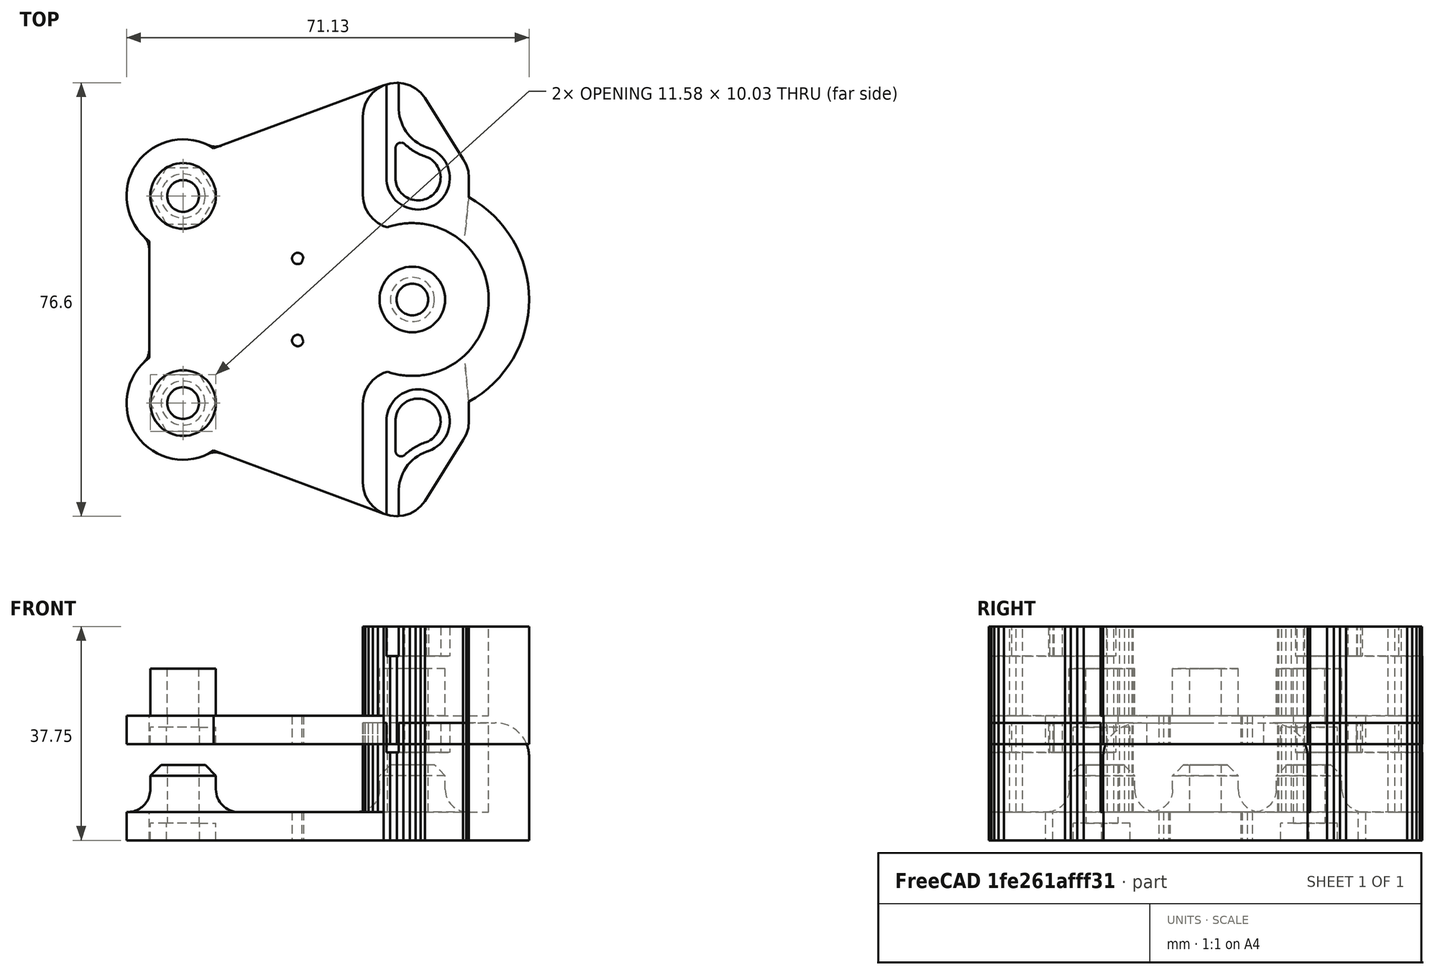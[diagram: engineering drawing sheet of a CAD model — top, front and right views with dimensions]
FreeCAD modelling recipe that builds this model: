
FCSTD DOCUMENT  (FreeCAD 0.19R24267 +99 (Git))
Label: carroX
License: All rights reserved
LicenseURL: http://en.wikipedia.org/wiki/All_rights_reserved
objects: Part::Feature×137, Part::Part2DObjectPython×10, Part::Cylinder×10, Part::FeaturePython×8, Part::Fillet×8, Part::Cut×7, Part::MultiFuse×6, Part::Extrusion×5, Part::Fuse×3, Part::Prism×3, Part::Box×1, App::DocumentObjectGroupPython×1, Part::Mirroring×1, Part::Refine×1, Part::Chamfer×1
note: 201 computed .brp shape members not serialized (recipe doc carries the construction recipe); baked Part::Feature solids carry a one-line shape summary decoded from their .brp

FEATURE [Part::Feature] polygon
  shape: bbox 44.5 x 64.6 x 2e-07 mm, 1 faces, 0 solids (baked)
FEATURE [Part::Part2DObjectPython] circle  # Draft 2D object (typed FeaturePython)
  Area = 113.097
  FirstAngle = 0
  LastAngle = 0
  MakeFace = true
  Radius = 6
FEATURE [Part::FeaturePython] minkowski  # WARN: FeaturePython — macro-defined, semantics opaque (R4)
  Arguments = {'convexity': '0'}
  Children = -> [polygon,circle]
  Operation = minkowski
FEATURE [Part::Part2DObjectPython] circle001  # Draft 2D object (typed FeaturePython)
  Area = 314.159
  FirstAngle = 0
  LastAngle = 0
  MakeFace = true
  Placement = pos=(-20.25,-18.3,0) rot=(0,0,1;0rad)
  Radius = 10
FEATURE [Part::Part2DObjectPython] circle002  # Draft 2D object (typed FeaturePython)
  Area = 314.159
  FirstAngle = 0
  LastAngle = 0
  MakeFace = true
  Placement = pos=(-20.25,18.3,0) rot=(0,0,1;0rad)
  Radius = 10
FEATURE [Part::MultiFuse] union
  Shapes = -> [minkowski,circle001,circle002]
FEATURE [Part::Part2DObjectPython] circle003  # Draft 2D object (typed FeaturePython)
  Area = 24.6301
  FirstAngle = 0
  LastAngle = 0
  MakeFace = true
  Placement = pos=(-20.25,-18.3,0) rot=(0,0,1;0rad)
  Radius = 2.8
FEATURE [Part::Part2DObjectPython] circle004  # Draft 2D object (typed FeaturePython)
  Area = 24.6301
  FirstAngle = 0
  LastAngle = 0
  MakeFace = true
  Placement = pos=(20.25,0,0) rot=(0,0,1;0rad)
  Radius = 2.8
FEATURE [Part::Part2DObjectPython] circle005  # Draft 2D object (typed FeaturePython)
  Area = 24.6301
  FirstAngle = 0
  LastAngle = 0
  MakeFace = true
  Placement = pos=(-20.25,18.3,0) rot=(0,0,1;0rad)
  Radius = 2.8
FEATURE [Part::Part2DObjectPython] circle006  # Draft 2D object (typed FeaturePython)
  Area = 3.14159
  FirstAngle = 0
  LastAngle = 0
  MakeFace = true
  Placement = pos=(0,7.25,0) rot=(0,0,1;0rad)
  Radius = 1
FEATURE [Part::Part2DObjectPython] circle007  # Draft 2D object (typed FeaturePython)
  Area = 3.14159
  FirstAngle = 0
  LastAngle = 0
  MakeFace = true
  Placement = pos=(0,-7.25,0) rot=(0,0,1;0rad)
  Radius = 1
FEATURE [Part::MultiFuse] union001
  Shapes = -> [circle003,circle004,circle005,circle006,circle007]
FEATURE [Part::Cut] difference
  Base = -> union
  Tool = -> union001
FEATURE [Part::FeaturePython] RefineLinearExtrude  # WARN: FeaturePython — macro-defined, semantics opaque (R4)
  Base = -> difference
FEATURE [Part::Extrusion] LinearExtrude
  Base = -> RefineLinearExtrude
  Dir = (0,0,5)
  DirMode = 0
  FaceMakerClass = Part::FaceMakerBullseye
  LengthFwd = 0
  LengthRev = 0
  Solid = false
  Symmetric = false
FEATURE [Part::Feature] polygon001
  shape: bbox 6.75 x 13.8 x 2e-07 mm, 1 faces, 0 solids (baked)
FEATURE [Part::Part2DObjectPython] circle008  # Draft 2D object (typed FeaturePython)
  Area = 113.097
  FirstAngle = 0
  LastAngle = 0
  MakeFace = true
  Radius = 6
FEATURE [Part::FeaturePython] minkowski001  # WARN: FeaturePython — macro-defined, semantics opaque (R4)
  Arguments = {'convexity': '0'}
  Children = -> [polygon001,circle008]
  Operation = minkowski
FEATURE [Part::FeaturePython] RefineLinearExtrude001  # WARN: FeaturePython — macro-defined, semantics opaque (R4)
  Base = -> minkowski001
FEATURE [Part::Extrusion] LinearExtrude001
  Base = -> RefineLinearExtrude001
  Dir = (0,0,20.75)
  DirMode = 0
  FaceMakerClass = Part::FaceMakerBullseye
  LengthFwd = 0
  LengthRev = 0
  Solid = false
  Symmetric = false
FEATURE [Part::Feature] polygon002
  shape: bbox 6.75 x 13.8 x 2e-07 mm, 1 faces, 0 solids (baked)
FEATURE [Part::Part2DObjectPython] circle009  # Draft 2D object (typed FeaturePython)
  Area = 113.097
  FirstAngle = 0
  LastAngle = 0
  MakeFace = true
  Radius = 6
FEATURE [Part::FeaturePython] minkowski002  # WARN: FeaturePython — macro-defined, semantics opaque (R4)
  Arguments = {'convexity': '0'}
  Children = -> [polygon002,circle009]
  Operation = minkowski
FEATURE [Part::FeaturePython] RefineLinearExtrude002  # WARN: FeaturePython — macro-defined, semantics opaque (R4)
  Base = -> minkowski002
FEATURE [Part::Extrusion] LinearExtrude002
  Base = -> RefineLinearExtrude002
  Dir = (0,0,20.75)
  DirMode = 0
  FaceMakerClass = Part::FaceMakerBullseye
  LengthFwd = 0
  LengthRev = 0
  Solid = false
  Symmetric = false
FEATURE [Part::Fuse] union002
  Base = -> LinearExtrude001
  Tool = -> LinearExtrude002
FEATURE [Part::Cylinder] cylinder
  Angle = 360
  AttacherType = Attacher::AttachEngine3D
  Height = 60
  Placement = pos=(20.25,0,0) rot=(0,0,1;0rad)
  Radius = 13.5
FEATURE [Part::Cut] difference001
  Base = -> union002
  Tool = -> cylinder
FEATURE [Part::Cylinder] cylinder001
  Angle = 360
  AttacherType = Attacher::AttachEngine3D
  Height = 13.3
  Radius = 5.8
FEATURE [Part::Cylinder] cylinder002
  Angle = 360
  AttacherType = Attacher::AttachEngine3D
  Height = 53.2
  Placement = pos=(0,0,-26.6) rot=(0,0,1;0rad)
  Radius = 2.8
FEATURE [Part::Cut] difference002
  Base = -> cylinder001
  Placement = pos=(-20.25,-18.3,0) rot=(0,0,1;0rad)
  Tool = -> cylinder002
FEATURE [Part::Cylinder] cylinder003
  Angle = 360
  AttacherType = Attacher::AttachEngine3D
  Height = 13.3
  Radius = 5.8
FEATURE [Part::Cylinder] cylinder004
  Angle = 360
  AttacherType = Attacher::AttachEngine3D
  Height = 53.2
  Placement = pos=(0,0,-26.6) rot=(0,0,1;0rad)
  Radius = 2.8
FEATURE [Part::Cut] difference003
  Base = -> cylinder003
  Placement = pos=(-20.25,18.3,0) rot=(0,0,1;0rad)
  Tool = -> cylinder004
FEATURE [Part::Cylinder] cylinder005
  Angle = 360
  AttacherType = Attacher::AttachEngine3D
  Height = 13.3
  Radius = 5.8
FEATURE [Part::Cylinder] cylinder006
  Angle = 360
  AttacherType = Attacher::AttachEngine3D
  Height = 53.2
  Placement = pos=(0,0,-26.6) rot=(0,0,1;0rad)
  Radius = 2.8
FEATURE [Part::Cut] difference004
  Base = -> cylinder005
  Placement = pos=(20.25,0,0) rot=(0,0,1;0rad)
  Tool = -> cylinder006
FEATURE [Part::Cylinder] cylinder007
  Angle = 360
  AttacherType = Attacher::AttachEngine3D
  Height = 20.75
  Radius = 20.625
FEATURE [Part::Cylinder] cylinder008
  Angle = 360
  AttacherType = Attacher::AttachEngine3D
  Height = 1000
  Placement = pos=(0,0,4.99) rot=(0,0,1;0rad)
  Radius = 13.5
FEATURE [Part::Box] cube
  AttacherType = Attacher::AttachEngine3D
  Height = 1000
  Length = 1000
  Placement = pos=(-1000,-500,0) rot=(0,0,1;0rad)
  Width = 1000
FEATURE [Part::Fuse] union003
  Base = -> cylinder008
  Tool = -> cube
FEATURE [Part::Cut] difference005
  Base = -> cylinder007
  Placement = pos=(20.25,0,0) rot=(0,0,1;0rad)
  Tool = -> union003
FEATURE [Part::MultiFuse] union004
  Shapes = -> [LinearExtrude,difference001,difference002,difference003,difference004,difference005]
FEATURE [Part::Prism] prism
  AttacherType = Attacher::AttachEngine3D
  Circumradius = 5.79
  FirstAngle = 0
  Height = 6
  Placement = pos=(-20.25,-18.3,-3) rot=(0,0,1;0rad)
  Polygon = 6
  SecondAngle = 0
FEATURE [Part::Prism] prism001
  AttacherType = Attacher::AttachEngine3D
  Circumradius = 5.79
  FirstAngle = 0
  Height = 6
  Placement = pos=(-20.25,18.3,-3) rot=(0,0,1;0rad)
  Polygon = 6
  SecondAngle = 0
FEATURE [Part::Prism] prism002
  AttacherType = Attacher::AttachEngine3D
  Circumradius = 5.79
  FirstAngle = 0
  Height = 6
  Placement = pos=(20.25,0,-3) rot=(0,0,1;0rad)
  Polygon = 6
  SecondAngle = 0
FEATURE [Part::MultiFuse] Group
  Shapes = -> [prism,prism001,prism002]
FEATURE [App::DocumentObjectGroupPython] LayerContainer  label="Capas"  # scripted group (container) (typed FeaturePython)
FEATURE [Part::Feature] Line
  shape: bbox 25.93 x 2e-07 x 2e-07 mm, 0 faces, 0 solids (baked)
FEATURE [Part::Feature] Line001
  shape: bbox 5.23 x 0.01028 x 2e-07 mm, 0 faces, 0 solids (baked)
FEATURE [Part::Feature] Line002
  shape: bbox 13.12 x 2e-07 x 2e-07 mm, 0 faces, 0 solids (baked)
FEATURE [Part::Feature] Line003
  shape: bbox 46.78 x 2e-07 x 2e-07 mm, 0 faces, 0 solids (baked)
FEATURE [Part::Feature] Line004
  shape: bbox 46.66 x 2e-07 x 2e-07 mm, 0 faces, 0 solids (baked)
FEATURE [Part::Feature] Line005
  shape: bbox 2e-07 x 2.2 x 2e-07 mm, 0 faces, 0 solids (baked)
FEATURE [Part::Feature] Arc
  shape: bbox 7.844 x 7.989 x 2e-07 mm, 0 faces, 0 solids (baked)
FEATURE [Part::Feature] Arc001
  shape: bbox 0.9979 x 1.743 x 2e-07 mm, 0 faces, 0 solids (baked)
FEATURE [Part::Feature] Arc002
  shape: bbox 10.99 x 11.2 x 2e-07 mm, 0 faces, 0 solids (baked)
FEATURE [Part::Feature] Arc003
  shape: bbox 2.238 x 3.76 x 2e-07 mm, 0 faces, 0 solids (baked)
FEATURE [Part::Feature] Arc004
  shape: bbox 7.439 x 5.334 x 2e-07 mm, 0 faces, 0 solids (baked)
FEATURE [Part::Feature] dxf_ToyRepCart_all
  Placement = pos=(0,0,0) rot=(0,0,1;1.5708rad)
  shape: bbox 11.2 x 78.19 x 2e-07 mm, 1 faces, 0 solids (baked)
FEATURE [Part::FeaturePython] RefineLinearExtrude003  # WARN: FeaturePython — macro-defined, semantics opaque (R4)
  Base = -> dxf_ToyRepCart_all
FEATURE [Part::Extrusion] LinearExtrude003
  Base = -> RefineLinearExtrude003
  Dir = (0,0,100)
  DirMode = 0
  FaceMakerClass = Part::FaceMakerBullseye
  LengthFwd = 0
  LengthRev = 0
  Placement = pos=(21.25,-21.5,15.55) rot=(0,0,1;0rad)
  Solid = false
  Symmetric = false
FEATURE [Part::Feature] Line006
  shape: bbox 25.93 x 2e-07 x 2e-07 mm, 0 faces, 0 solids (baked)
FEATURE [Part::Feature] Line007
  shape: bbox 5.23 x 0.01028 x 2e-07 mm, 0 faces, 0 solids (baked)
FEATURE [Part::Feature] Line008
  shape: bbox 13.12 x 2e-07 x 2e-07 mm, 0 faces, 0 solids (baked)
FEATURE [Part::Feature] Line009
  shape: bbox 46.78 x 2e-07 x 2e-07 mm, 0 faces, 0 solids (baked)
FEATURE [Part::Feature] Line010
  shape: bbox 46.66 x 2e-07 x 2e-07 mm, 0 faces, 0 solids (baked)
FEATURE [Part::Feature] Line011
  shape: bbox 2e-07 x 2.2 x 2e-07 mm, 0 faces, 0 solids (baked)
FEATURE [Part::Feature] Arc005
  shape: bbox 7.844 x 7.989 x 2e-07 mm, 0 faces, 0 solids (baked)
FEATURE [Part::Feature] Arc006
  shape: bbox 0.9979 x 1.743 x 2e-07 mm, 0 faces, 0 solids (baked)
FEATURE [Part::Feature] Arc007
  shape: bbox 10.99 x 11.2 x 2e-07 mm, 0 faces, 0 solids (baked)
FEATURE [Part::Feature] Arc008
  shape: bbox 2.238 x 3.76 x 2e-07 mm, 0 faces, 0 solids (baked)
FEATURE [Part::Feature] Arc009
  shape: bbox 7.439 x 5.334 x 2e-07 mm, 0 faces, 0 solids (baked)
FEATURE [Part::Feature] dxf_ToyRepCart_all001
  Placement = pos=(0,0,0) rot=(0,0,1;1.5708rad)
  shape: bbox 11.2 x 78.19 x 2e-07 mm, 1 faces, 0 solids (baked)
FEATURE [Part::FeaturePython] RefineLinearExtrude004  # WARN: FeaturePython — macro-defined, semantics opaque (R4)
  Base = -> dxf_ToyRepCart_all001
FEATURE [Part::Extrusion] LinearExtrude004
  Base = -> RefineLinearExtrude004
  Dir = (0,0,100)
  DirMode = 0
  FaceMakerClass = Part::FaceMakerBullseye
  LengthFwd = 0
  LengthRev = 0
  Placement = pos=(21.25,-21.5,15.55) rot=(0,0,1;0rad)
  Solid = false
  Symmetric = false
FEATURE [Part::Mirroring] mirr_LinearExtrude004  label="mirrored LinearExtrude004"
  Base = (0,0,0)
  Normal = (0,1,0)
  Source = -> LinearExtrude004
FEATURE [Part::MultiFuse] union005
  Shapes = -> [Group,LinearExtrude003,mirr_LinearExtrude004]
FEATURE [Part::Cut] difference006
  Base = -> union004
  Tool = -> union005
FEATURE [Part::Cylinder] cylinder009
  Angle = 360
  AttacherType = Attacher::AttachEngine3D
  Height = 5
  Placement = pos=(20.25,0,0) rot=(0,0,1;0rad)
  Radius = 20.625
FEATURE [Part::Fuse] Group001
  Base = -> difference006
  Tool = -> cylinder009
FEATURE [Part::Feature] Line012
  shape: bbox 1.171 x 0.1152 x 2e-07 mm, 0 faces, 0 solids (baked)
FEATURE [Part::Feature] Line013
  shape: bbox 1.171 x 0.1152 x 2e-07 mm, 0 faces, 0 solids (baked)
FEATURE [Part::Feature] Line014
  shape: bbox 1.125 x 0.3418 x 2e-07 mm, 0 faces, 0 solids (baked)
FEATURE [Part::Feature] Line015
  shape: bbox 37.75 x 14 x 2e-07 mm, 0 faces, 0 solids (baked)
FEATURE [Part::Feature] Line016
  shape: bbox 1.037 x 0.5537 x 2e-07 mm, 0 faces, 0 solids (baked)
FEATURE [Part::Feature] Line017
  shape: bbox 0.9092 x 0.7471 x 2e-07 mm, 0 faces, 0 solids (baked)
FEATURE [Part::Feature] Line018
  shape: bbox 0.7471 x 0.9092 x 2e-07 mm, 0 faces, 0 solids (baked)
FEATURE [Part::Feature] Line019
  shape: bbox 0.5537 x 1.037 x 2e-07 mm, 0 faces, 0 solids (baked)
FEATURE [Part::Feature] Line020
  shape: bbox 0.3418 x 1.125 x 2e-07 mm, 0 faces, 0 solids (baked)
FEATURE [Part::Feature] Line021
  shape: bbox 0.1152 x 1.171 x 2e-07 mm, 0 faces, 0 solids (baked)
FEATURE [Part::Feature] Line022
  shape: bbox 2e-07 x 36.6 x 2e-07 mm, 0 faces, 0 solids (baked)
FEATURE [Part::Feature] Line023
  shape: bbox 0.1152 x 1.171 x 2e-07 mm, 0 faces, 0 solids (baked)
FEATURE [Part::Feature] Line024
  shape: bbox 0.3418 x 1.125 x 2e-07 mm, 0 faces, 0 solids (baked)
FEATURE [Part::Feature] Line025
  shape: bbox 0.5537 x 1.037 x 2e-07 mm, 0 faces, 0 solids (baked)
FEATURE [Part::Feature] Line026
  shape: bbox 0.7471 x 0.9092 x 2e-07 mm, 0 faces, 0 solids (baked)
FEATURE [Part::Feature] Line027
  shape: bbox 0.9092 x 0.7471 x 2e-07 mm, 0 faces, 0 solids (baked)
FEATURE [Part::Feature] Line028
  shape: bbox 1.037 x 0.5537 x 2e-07 mm, 0 faces, 0 solids (baked)
FEATURE [Part::Feature] Line029
  shape: bbox 37.75 x 14 x 2e-07 mm, 0 faces, 0 solids (baked)
FEATURE [Part::Feature] Line030
  shape: bbox 1.125 x 0.3418 x 2e-07 mm, 0 faces, 0 solids (baked)
FEATURE [Part::Feature] Line031
  shape: bbox 1.171 x 0.1152 x 2e-07 mm, 0 faces, 0 solids (baked)
FEATURE [Part::Feature] Line032
  shape: bbox 1.171 x 0.1152 x 2e-07 mm, 0 faces, 0 solids (baked)
FEATURE [Part::Feature] Line033
  shape: bbox 1.125 x 0.3418 x 2e-07 mm, 0 faces, 0 solids (baked)
FEATURE [Part::Feature] Line034
  shape: bbox 1.037 x 0.5537 x 2e-07 mm, 0 faces, 0 solids (baked)
FEATURE [Part::Feature] Line035
  shape: bbox 0.9092 x 0.7471 x 2e-07 mm, 0 faces, 0 solids (baked)
FEATURE [Part::Feature] Line036
  shape: bbox 0.7471 x 0.9092 x 2e-07 mm, 0 faces, 0 solids (baked)
FEATURE [Part::Feature] Line037
  shape: bbox 6.75 x 10.8 x 2e-07 mm, 0 faces, 0 solids (baked)
FEATURE [Part::Feature] Line038
  shape: bbox 0.5537 x 1.037 x 2e-07 mm, 0 faces, 0 solids (baked)
FEATURE [Part::Feature] Line039
  shape: bbox 0.3418 x 1.125 x 2e-07 mm, 0 faces, 0 solids (baked)
FEATURE [Part::Feature] Line040
  shape: bbox 0.1152 x 1.171 x 2e-07 mm, 0 faces, 0 solids (baked)
FEATURE [Part::Feature] Line041
  shape: bbox 2e-07 x 43 x 2e-07 mm, 0 faces, 0 solids (baked)
FEATURE [Part::Feature] Line042
  shape: bbox 0.1152 x 1.171 x 2e-07 mm, 0 faces, 0 solids (baked)
FEATURE [Part::Feature] Line043
  shape: bbox 0.3418 x 1.125 x 2e-07 mm, 0 faces, 0 solids (baked)
FEATURE [Part::Feature] Line044
  shape: bbox 0.5537 x 1.037 x 2e-07 mm, 0 faces, 0 solids (baked)
FEATURE [Part::Feature] Line045
  shape: bbox 6.75 x 10.8 x 2e-07 mm, 0 faces, 0 solids (baked)
FEATURE [Part::Feature] Line046
  shape: bbox 0.7471 x 0.9092 x 2e-07 mm, 0 faces, 0 solids (baked)
FEATURE [Part::Feature] Line047
  shape: bbox 0.9092 x 0.7471 x 2e-07 mm, 0 faces, 0 solids (baked)
FEATURE [Part::Feature] Line048
  shape: bbox 1.037 x 0.5537 x 2e-07 mm, 0 faces, 0 solids (baked)
FEATURE [Part::Feature] Line049
  shape: bbox 1.125 x 0.3418 x 2e-07 mm, 0 faces, 0 solids (baked)
FEATURE [Part::Feature] Line050
  shape: bbox 1.125 x 0.3418 x 2e-07 mm, 0 faces, 0 solids (baked)
FEATURE [Part::Feature] Line051
  shape: bbox 1.171 x 0.1152 x 2e-07 mm, 0 faces, 0 solids (baked)
FEATURE [Part::Feature] Line052
  shape: bbox 1.171 x 0.1152 x 2e-07 mm, 0 faces, 0 solids (baked)
FEATURE [Part::Feature] Line053
  shape: bbox 1.125 x 0.3418 x 2e-07 mm, 0 faces, 0 solids (baked)
FEATURE [Part::Feature] Line054
  shape: bbox 1.037 x 0.5537 x 2e-07 mm, 0 faces, 0 solids (baked)
FEATURE [Part::Feature] Line055
  shape: bbox 0.9092 x 0.7471 x 2e-07 mm, 0 faces, 0 solids (baked)
FEATURE [Part::Feature] Line056
  shape: bbox 0.7471 x 0.9092 x 2e-07 mm, 0 faces, 0 solids (baked)
FEATURE [Part::Feature] Line057
  shape: bbox 0.5537 x 1.037 x 2e-07 mm, 0 faces, 0 solids (baked)
FEATURE [Part::Feature] Line058
  shape: bbox 0.3418 x 1.125 x 2e-07 mm, 0 faces, 0 solids (baked)
FEATURE [Part::Feature] Line059
  shape: bbox 0.1152 x 1.171 x 2e-07 mm, 0 faces, 0 solids (baked)
FEATURE [Part::Feature] Line060
  shape: bbox 2e-07 x 13.8 x 2e-07 mm, 0 faces, 0 solids (baked)
FEATURE [Part::Feature] Line061
  shape: bbox 0.1152 x 1.171 x 2e-07 mm, 0 faces, 0 solids (baked)
FEATURE [Part::Feature] Line062
  shape: bbox 0.3418 x 1.125 x 2e-07 mm, 0 faces, 0 solids (baked)
FEATURE [Part::Feature] Line063
  shape: bbox 0.5537 x 1.037 x 2e-07 mm, 0 faces, 0 solids (baked)
FEATURE [Part::Feature] Line064
  shape: bbox 0.7471 x 0.9092 x 2e-07 mm, 0 faces, 0 solids (baked)
FEATURE [Part::Feature] Line065
  shape: bbox 0.9092 x 0.7471 x 2e-07 mm, 0 faces, 0 solids (baked)
FEATURE [Part::Feature] Line066
  shape: bbox 1.037 x 0.5537 x 2e-07 mm, 0 faces, 0 solids (baked)
FEATURE [Part::Feature] Line067
  shape: bbox 1.125 x 0.3418 x 2e-07 mm, 0 faces, 0 solids (baked)
FEATURE [Part::Feature] Line068
  shape: bbox 1.171 x 0.1152 x 2e-07 mm, 0 faces, 0 solids (baked)
FEATURE [Part::Feature] Line069
  shape: bbox 6.75 x 2e-07 x 2e-07 mm, 0 faces, 0 solids (baked)
FEATURE [Part::Feature] Line070
  shape: bbox 1.171 x 0.1152 x 2e-07 mm, 0 faces, 0 solids (baked)
FEATURE [Part::Feature] Line071
  shape: bbox 1.125 x 0.3418 x 2e-07 mm, 0 faces, 0 solids (baked)
FEATURE [Part::Feature] Line072
  shape: bbox 1.037 x 0.5537 x 2e-07 mm, 0 faces, 0 solids (baked)
FEATURE [Part::Feature] Line073
  shape: bbox 0.9092 x 0.7471 x 2e-07 mm, 0 faces, 0 solids (baked)
FEATURE [Part::Feature] Line074
  shape: bbox 0.7471 x 0.9092 x 2e-07 mm, 0 faces, 0 solids (baked)
FEATURE [Part::Feature] Line075
  shape: bbox 0.5537 x 1.037 x 2e-07 mm, 0 faces, 0 solids (baked)
FEATURE [Part::Feature] Line076
  shape: bbox 0.3418 x 1.125 x 2e-07 mm, 0 faces, 0 solids (baked)
FEATURE [Part::Feature] Line077
  shape: bbox 0.1152 x 1.171 x 2e-07 mm, 0 faces, 0 solids (baked)
FEATURE [Part::Feature] Line078
  shape: bbox 2e-07 x 3 x 2e-07 mm, 0 faces, 0 solids (baked)
FEATURE [Part::Feature] Line079
  shape: bbox 0.1152 x 1.171 x 2e-07 mm, 0 faces, 0 solids (baked)
FEATURE [Part::Feature] Line080
  shape: bbox 0.3418 x 1.125 x 2e-07 mm, 0 faces, 0 solids (baked)
FEATURE [Part::Feature] Line081
  shape: bbox 0.5537 x 1.037 x 2e-07 mm, 0 faces, 0 solids (baked)
FEATURE [Part::Feature] Line082
  shape: bbox 6.75 x 10.8 x 2e-07 mm, 0 faces, 0 solids (baked)
FEATURE [Part::Feature] Line083
  shape: bbox 0.7471 x 0.9092 x 2e-07 mm, 0 faces, 0 solids (baked)
FEATURE [Part::Feature] Line084
  shape: bbox 0.9092 x 0.7471 x 2e-07 mm, 0 faces, 0 solids (baked)
FEATURE [Part::Feature] Line085
  shape: bbox 1.037 x 0.5537 x 2e-07 mm, 0 faces, 0 solids (baked)
FEATURE [Part::Feature] Line086
  shape: bbox 0.7471 x 0.9092 x 2e-07 mm, 0 faces, 0 solids (baked)
FEATURE [Part::Feature] Line087
  shape: bbox 0.9092 x 0.7471 x 2e-07 mm, 0 faces, 0 solids (baked)
FEATURE [Part::Feature] Line088
  shape: bbox 1.037 x 0.5537 x 2e-07 mm, 0 faces, 0 solids (baked)
FEATURE [Part::Feature] Line089
  shape: bbox 1.125 x 0.3418 x 2e-07 mm, 0 faces, 0 solids (baked)
FEATURE [Part::Feature] Line090
  shape: bbox 1.171 x 0.1152 x 2e-07 mm, 0 faces, 0 solids (baked)
FEATURE [Part::Feature] Line091
  shape: bbox 6.75 x 2e-07 x 2e-07 mm, 0 faces, 0 solids (baked)
FEATURE [Part::Feature] Line092
  shape: bbox 1.171 x 0.1152 x 2e-07 mm, 0 faces, 0 solids (baked)
FEATURE [Part::Feature] Line093
  shape: bbox 1.125 x 0.3418 x 2e-07 mm, 0 faces, 0 solids (baked)
FEATURE [Part::Feature] Line094
  shape: bbox 1.037 x 0.5537 x 2e-07 mm, 0 faces, 0 solids (baked)
FEATURE [Part::Feature] Line095
  shape: bbox 0.9092 x 0.7471 x 2e-07 mm, 0 faces, 0 solids (baked)
FEATURE [Part::Feature] Line096
  shape: bbox 0.7471 x 0.9092 x 2e-07 mm, 0 faces, 0 solids (baked)
FEATURE [Part::Feature] Line097
  shape: bbox 0.5537 x 1.037 x 2e-07 mm, 0 faces, 0 solids (baked)
FEATURE [Part::Feature] Line098
  shape: bbox 0.3418 x 1.125 x 2e-07 mm, 0 faces, 0 solids (baked)
FEATURE [Part::Feature] Line099
  shape: bbox 0.1152 x 1.171 x 2e-07 mm, 0 faces, 0 solids (baked)
FEATURE [Part::Feature] Line100
  shape: bbox 2e-07 x 13.8 x 2e-07 mm, 0 faces, 0 solids (baked)
FEATURE [Part::Feature] Line101
  shape: bbox 0.1152 x 1.171 x 2e-07 mm, 0 faces, 0 solids (baked)
FEATURE [Part::Feature] Line102
  shape: bbox 0.3418 x 1.125 x 2e-07 mm, 0 faces, 0 solids (baked)
FEATURE [Part::Feature] Line103
  shape: bbox 0.5537 x 1.037 x 2e-07 mm, 0 faces, 0 solids (baked)
FEATURE [Part::Feature] Line104
  shape: bbox 0.7471 x 0.9092 x 2e-07 mm, 0 faces, 0 solids (baked)
FEATURE [Part::Feature] Line105
  shape: bbox 0.9092 x 0.7471 x 2e-07 mm, 0 faces, 0 solids (baked)
FEATURE [Part::Feature] Line106
  shape: bbox 1.037 x 0.5537 x 2e-07 mm, 0 faces, 0 solids (baked)
FEATURE [Part::Feature] Line107
  shape: bbox 1.125 x 0.3418 x 2e-07 mm, 0 faces, 0 solids (baked)
FEATURE [Part::Feature] Line108
  shape: bbox 1.171 x 0.1152 x 2e-07 mm, 0 faces, 0 solids (baked)
FEATURE [Part::Feature] Line109
  shape: bbox 1.171 x 0.1152 x 2e-07 mm, 0 faces, 0 solids (baked)
FEATURE [Part::Feature] Line110
  shape: bbox 1.125 x 0.3418 x 2e-07 mm, 0 faces, 0 solids (baked)
FEATURE [Part::Feature] Line111
  shape: bbox 1.037 x 0.5537 x 2e-07 mm, 0 faces, 0 solids (baked)
FEATURE [Part::Feature] Line112
  shape: bbox 0.9092 x 0.7471 x 2e-07 mm, 0 faces, 0 solids (baked)
FEATURE [Part::Feature] Line113
  shape: bbox 0.7471 x 0.9092 x 2e-07 mm, 0 faces, 0 solids (baked)
FEATURE [Part::Feature] Line114
  shape: bbox 6.75 x 10.8 x 2e-07 mm, 0 faces, 0 solids (baked)
FEATURE [Part::Feature] Line115
  shape: bbox 0.5537 x 1.037 x 2e-07 mm, 0 faces, 0 solids (baked)
FEATURE [Part::Feature] Line116
  shape: bbox 0.3418 x 1.125 x 2e-07 mm, 0 faces, 0 solids (baked)
FEATURE [Part::Feature] Line117
  shape: bbox 0.1152 x 1.171 x 2e-07 mm, 0 faces, 0 solids (baked)
FEATURE [Part::Feature] Line118
  shape: bbox 2e-07 x 3 x 2e-07 mm, 0 faces, 0 solids (baked)
FEATURE [Part::Feature] Line119
  shape: bbox 0.1152 x 1.171 x 2e-07 mm, 0 faces, 0 solids (baked)
FEATURE [Part::Feature] Line120
  shape: bbox 0.3418 x 1.125 x 2e-07 mm, 0 faces, 0 solids (baked)
FEATURE [Part::Feature] Line121
  shape: bbox 0.5537 x 1.037 x 2e-07 mm, 0 faces, 0 solids (baked)
FEATURE [Part::MultiFuse] Fusion
  Shapes = -> [difference006,cylinder009]
FEATURE [Part::Refine] Fusion001
  Source = -> Fusion
FEATURE [Part::Chamfer] Chamfer
  Base = -> Fusion001
  Edges = 3 edges r=1.9: [Edge266,Edge271,Edge274]
FEATURE [Part::Fillet] Fillet
  Base = -> Chamfer
  Edges = 1 edges r=4: [Edge47]
FEATURE [Part::Fillet] Fillet001
  Base = -> Fillet
  Edges = 1 edges r=4: [Edge44]
FEATURE [Part::Fillet] Fillet002
  Base = -> Fillet001
  Edges = 1 edges r=4: [Edge44]
  Placement = pos=(0,0,-17) rot=(0,0,1;0rad)
FEATURE [Part::Fillet] Fillet003
  Base = -> Fillet002
  Edges = 1 edges r=3: [Edge67]
FEATURE [Part::Fillet] Fillet004
  Base = -> Fillet003
  Edges = 1 edges r=3: [Edge52]
FEATURE [Part::Fillet] Fillet005
  Base = -> Fillet004
  Edges = 1 edges r=3: [Edge59]
FEATURE [Part::Fillet] Fillet006
  Base = -> Fillet005
  Edges = 1 edges r=3: [Edge54]
FEATURE [Part::Fillet] Fillet007
  Base = -> Fillet006
  Edges = 1 edges r=6: [Edge223]
